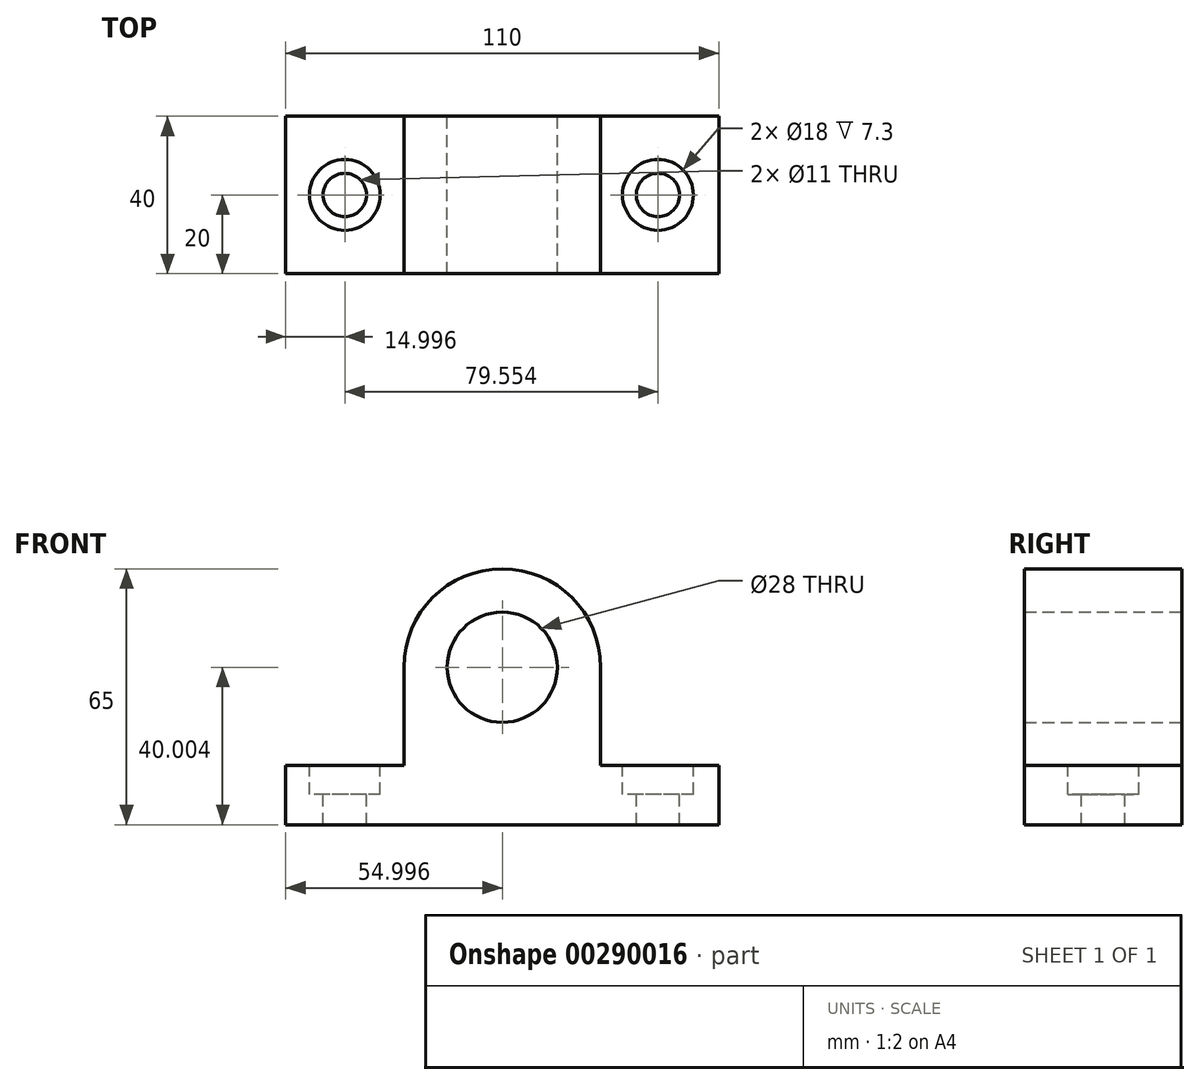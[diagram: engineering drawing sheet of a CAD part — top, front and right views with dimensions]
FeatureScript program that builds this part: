
annotation { "Feature Type Name" : "Feature", "Feature Type Description" : "" }
export const myFeature = defineFeature(function(context is Context, id is Id, definition is map)
    precondition{}
    {
        {
            var Q0;
            Q0=qCreatedBy(makeId("Front.planeOp"),FACE);
            var sketch = newSketch(context, id + "F0", { "sketchPlane" : qUnion([Q0])});
            skLineSegment(sketch, "E0", {"start": v(-39.55, 15.71) * mm, "end": v(-39.55, -49.29) * mm, "construction": true});
            skLineSegment(sketch, "E1", {"start": v(-64.55, -9.29) * mm, "end": v(-14.55, -9.29) * mm, "construction": true});
            skArc(sketch, "E2", {"start": v(-14.55, -9.29) * mm, "mid": v(-39.55, 15.71) * mm, "end": v(-64.55, -9.29) * mm});
            skPoint(sketch, "E2.centerSnap0", {"position": v(-35.85, -9.29) * mm});
            skLineSegment(sketch, "E3", {"start": v(-64.55, -9.29) * mm, "end": v(-64.55, -34.29) * mm});
            skLineSegment(sketch, "E4", {"start": v(-64.55, -34.29) * mm, "end": v(-94.55, -34.29) * mm});
            skLineSegment(sketch, "E5", {"start": v(-94.55, -34.29) * mm, "end": v(-94.55, -49.29) * mm});
            skLineSegment(sketch, "E6", {"start": v(-94.55, -49.29) * mm, "end": v(15.45, -49.29) * mm});
            skLineSegment(sketch, "E7", {"start": v(15.45, -49.29) * mm, "end": v(15.45, -34.29) * mm});
            skLineSegment(sketch, "E8", {"start": v(15.45, -34.29) * mm, "end": v(-14.55, -34.29) * mm});
            skLineSegment(sketch, "E9", {"start": v(-14.55, -9.29) * mm, "end": v(-14.55, -34.29) * mm});
            skPoint(sketch, "E10.orphan", {"position": v(-14.55, -54.82) * mm});
            skCircle(sketch, "E11", {"center": v(-39.55, -9.29) * mm, "radius": 14 * mm});
            skPoint(sketch, "E12.orphan", {"position": v(-71.7, -9.29) * mm});
            skPoint(sketch, "E13.orphan", {"position": v(0, -9.29) * mm});
            skPoint(sketch, "E14.orphan", {"position": v(-39.55, -54.82) * mm});
            skSolve(sketch);
        }
        {
            var Q0;
            Q0=makeQuery(id+"F0.imprint","IMPRINT",FACE,{"disambiguationData":[TD([[makeQuery(id+"F0.imprint","IMPRINT",EDGE,{"derivedFrom":sQuery(id+"F0.wireOp",EDGE,"E2")}),1.0]])]});
            extrude(context, id + "F1", {"entities" : qUnion([Q0]), "depth" : 40 * mm});
        }
        {
            var Q0;
            Q0=makeQuery(id+"F1.opExtrude","SWEPT_FACE",FACE,{"disambiguationData":[OSD([sQuery(id+"F0.wireOp",EDGE,"E4")])]});
            var sketch = newSketch(context, id + "F2", { "sketchPlane" : qUnion([Q0])});
            skLineSegment(sketch, "E15", {"start": v(-79.55, -11) * mm, "end": v(-79.55, -29) * mm, "construction": true});
            skPoint(sketch, "E16.start.orphan", {"position": v(-94.55, 9.64) * mm});
            skLineSegment(sketch, "E17", {"start": v(-88.55, -20) * mm, "end": v(-70.55, -20) * mm, "construction": true});
            skPoint(sketch, "E18.start.orphan", {"position": v(-102.72, 0) * mm});
            skCircle(sketch, "E19", {"center": v(-79.55, -20) * mm, "radius": 9 * mm});
            skPoint(sketch, "E20.start.orphan", {"position": v(0, 11.79) * mm});
            skLineSegment(sketch, "E21", {"start": v(0, -11) * mm, "end": v(0, -29) * mm, "construction": true});
            skCircle(sketch, "E22", {"center": v(0, -20) * mm, "radius": 9 * mm});
            skCircle(sketch, "E23", {"center": v(-79.55, -20) * mm, "radius": 5.5 * mm});
            skCircle(sketch, "E24", {"center": v(0, -20) * mm, "radius": 5.5 * mm});
            skLineSegment(sketch, "E25.trimOffspring", {"start": v(-9, -20) * mm, "end": v(9, -20) * mm, "construction": true});
            skSolve(sketch);
        }
        {
            var Q0;
            Q0=makeQuery(id+"F2.imprint","IMPRINT",FACE,{"disambiguationData":[TD([[makeQuery(id+"F2.imprint","IMPRINT",EDGE,{"derivedFrom":sQuery(id+"F2.wireOp",EDGE,"E19")}),1.0]])]});
            var Q1;
            Q1=makeQuery(id+"F2.imprint","IMPRINT",FACE,{"disambiguationData":[TD([[makeQuery(id+"F2.imprint","IMPRINT",EDGE,{"derivedFrom":sQuery(id+"F2.wireOp",EDGE,"E22")}),1.0]])]});
            extrude(context, id + "F3", {"entities" : qUnion([Q0, Q1]), "operationType" : NewBodyOperationType.REMOVE, "oppositeDirection" : true, "depth" : 7.3 * mm});
        }
        {
            var Q0;
            Q0=makeQuery(id+"F2.imprint","IMPRINT",FACE,{"disambiguationData":[TD([[makeQuery(id+"F2.imprint","IMPRINT",EDGE,{"derivedFrom":sQuery(id+"F2.wireOp",EDGE,"E23")}),1.0]])]});
            var Q1;
            Q1=makeQuery(id+"F2.imprint","IMPRINT",FACE,{"disambiguationData":[TD([[makeQuery(id+"F2.imprint","IMPRINT",EDGE,{"derivedFrom":sQuery(id+"F2.wireOp",EDGE,"E24")}),1.0]])]});
            var Q2;
            Q2=sQuery(id+"F2.wireOp",EDGE,"E23");
            var Q3;
            Q3=sQuery(id+"F2.wireOp",EDGE,"E24");
            extrude(context, id + "F4", {"entities" : qUnion([Q0, Q1]), "operationType" : NewBodyOperationType.REMOVE, "surfaceEntities" : qUnion([Q2, Q3]), "oppositeDirection" : true, "depth" : 25 * mm});
        }
    });
